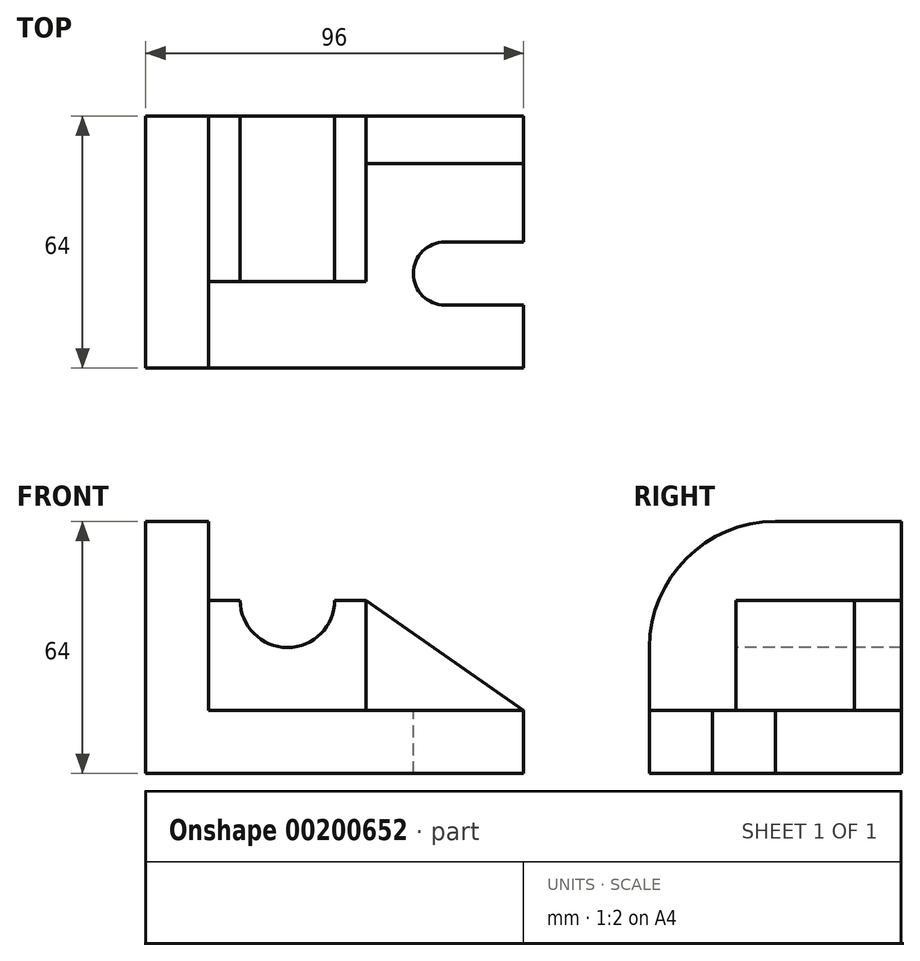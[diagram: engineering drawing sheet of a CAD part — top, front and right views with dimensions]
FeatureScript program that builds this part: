
annotation { "Feature Type Name" : "Feature", "Feature Type Description" : "" }
export const myFeature = defineFeature(function(context is Context, id is Id, definition is map)
    precondition{}
    {
        {
            var Q0;
            Q0=qCreatedBy(makeId("Front.planeOp"),FACE);
            var sketch = newSketch(context, id + "F0", { "sketchPlane" : qUnion([Q0])});
            skLineSegment(sketch, "E0.bottom", {"start": v(-41.26, -23.63) * mm, "end": v(54.74, -23.63) * mm});
            skLineSegment(sketch, "E0.top", {"start": v(-41.26, -39.63) * mm, "end": v(54.74, -39.63) * mm});
            skLineSegment(sketch, "E0.left", {"start": v(-41.26, -23.63) * mm, "end": v(-41.26, -39.63) * mm});
            skLineSegment(sketch, "E0.right", {"start": v(54.74, -23.63) * mm, "end": v(54.74, -39.63) * mm});
            skLineSegment(sketch, "E1.bottom", {"start": v(-41.26, -23.63) * mm, "end": v(-25.26, -23.63) * mm});
            skLineSegment(sketch, "E1.top", {"start": v(-41.26, 24.37) * mm, "end": v(-25.26, 24.37) * mm});
            skLineSegment(sketch, "E1.left", {"start": v(-41.26, -23.63) * mm, "end": v(-41.26, 24.37) * mm});
            skLineSegment(sketch, "E1.right", {"start": v(-25.26, -23.63) * mm, "end": v(-25.26, 24.37) * mm});
            skSolve(sketch);
        }
        {
            var Q0;
            Q0 = qSketchRegion(id + "F0", true);
            extrude(context, id + "F1", {"entities" : qUnion([Q0]), "depth" : 64 * mm});
        }
        {
            var Q0;
            Q0=makeQuery(id+"F1.opExtrude","CAP_EDGE",EDGE,{"disambiguationData":[OSD([sQuery(id+"F0.wireOp",EDGE,"E1.top")])],"isStart":false});
            fillet(context, id + "F2", {"entities" : qUnion([Q0]), "radius" : 32 * mm, "tangentPropagation" : true, "allowEdgeOverflow" : false});
        }
        {
            var Q0;
            Q0=makeQuery(id+"F1.opExtrude","SWEPT_FACE",FACE,{"disambiguationData":[OSD([sQuery(id+"F0.wireOp",EDGE,"E0.bottom")])]});
            var sketch = newSketch(context, id + "F3", { "sketchPlane" : qUnion([Q0])});
            skArc(sketch, "E2", {"start": v(34.74, -32) * mm, "mid": v(26.74, -40) * mm, "end": v(34.74, -48) * mm});
            skLineSegment(sketch, "E3.bottom", {"start": v(54.74, -32) * mm, "end": v(34.74, -32) * mm});
            skLineSegment(sketch, "E3.top", {"start": v(54.74, -48) * mm, "end": v(34.74, -48) * mm});
            skLineSegment(sketch, "E3.left", {"start": v(54.74, -32) * mm, "end": v(54.74, -48) * mm});
            skPoint(sketch, "E3.right.end.orphan", {"position": v(14.74, -48) * mm});
            skPoint(sketch, "E3.right.start.orphan", {"position": v(14.74, -32) * mm});
            skLineSegment(sketch, "E4.bottom", {"start": v(-25.26, 0) * mm, "end": v(14.74, 0) * mm});
            skLineSegment(sketch, "E4.top", {"start": v(-25.26, -42) * mm, "end": v(14.74, -42) * mm});
            skLineSegment(sketch, "E4.left", {"start": v(-25.26, 0) * mm, "end": v(-25.26, -42) * mm});
            skLineSegment(sketch, "E4.right", {"start": v(14.74, 0) * mm, "end": v(14.74, -42) * mm});
            skSolve(sketch);
        }
        {
            var Q0;
            Q0=makeQuery(id+"F3.imprint","IMPRINT",FACE,{"disambiguationData":[TD([[makeQuery(id+"F3.imprint","IMPRINT",EDGE,{"derivedFrom":sQuery(id+"F3.wireOp",EDGE,"E2")}),1.0]])]});
            extrude(context, id + "F4", {"entities" : qUnion([Q0]), "operationType" : NewBodyOperationType.REMOVE, "endBound" : BoundingType.UP_TO_NEXT, "oppositeDirection" : true, "depth" : 25 * mm});
        }
        {
            var Q0;
            Q0=makeQuery(id+"F3.imprint","IMPRINT",FACE,{"disambiguationData":[TD([[makeQuery(id+"F3.imprint","IMPRINT",EDGE,{"derivedFrom":sQuery(id+"F3.wireOp",EDGE,"E4.bottom")}),-1.0]])]});
            extrude(context, id + "F5", {"entities" : qUnion([Q0]), "operationType" : NewBodyOperationType.ADD, "depth" : 28 * mm});
        }
        {
            var Q0;
            Q0=makeQuery(id+"F5.opExtrude","SWEPT_FACE",FACE,{"disambiguationData":[OSD([sQuery(id+"F3.wireOp",EDGE,"E4.top")])]});
            var sketch = newSketch(context, id + "F6", { "sketchPlane" : qUnion([Q0])});
            skCircle(sketch, "E5", {"center": v(-5.26, 4.37) * mm, "radius": 12 * mm});
            skSolve(sketch);
        }
        {
            var Q0;
            {var subQ0=sQuery(id+"F6.wireOp",EDGE,"E5");var subQ1=makeQuery(id+"F5.opExtrude","CAP_EDGE",EDGE,{"disambiguationData":[OSD([sQuery(id+"F3.wireOp",EDGE,"E4.top")])],"isStart":false});var subQ2=makeQuery(id+"F6.imprint","INTERSECT",VERTEX,{"disambiguationData":[OD(0.0)],"derivedFrom":[subQ1,subQ0]});Q0=makeQuery(id+"F6.imprint","IMPRINT",FACE,{"disambiguationData":[TD([[makeQuery(id+"F6.imprint","IMPRINT",EDGE,{"disambiguationData":[TD([[subQ2,1.0]])],"derivedFrom":subQ0}),1.0]])]});}
            extrude(context, id + "F7", {"entities" : qUnion([Q0]), "operationType" : NewBodyOperationType.REMOVE, "oppositeDirection" : true, "depth" : 42 * mm, "hasSecondDirection" : true, "secondDirectionOppositeDirection" : false, "secondDirectionDepth" : 25 * mm});
        }
        {
            var Q0;
            Q0=makeQuery(id+"F5.boolean.opBoolean","MERGE",FACE,{"derivedFrom":[makeQuery(id+"F1.opExtrude","CAP_FACE",FACE,{"disambiguationData":[OSD([sQuery(id+"F0.wireOp",EDGE,"E0.bottom"),sQuery(id+"F0.wireOp",EDGE,"E0.top"),sQuery(id+"F0.wireOp",EDGE,"E0.left"),sQuery(id+"F0.wireOp",EDGE,"E0.right"),sQuery(id+"F0.wireOp",EDGE,"E1.top"),sQuery(id+"F0.wireOp",EDGE,"E1.left"),sQuery(id+"F0.wireOp",EDGE,"E1.right")])],"isStart":true}),makeQuery(id+"F5.opExtrude","SWEPT_FACE",FACE,{"disambiguationData":[OSD([sQuery(id+"F3.wireOp",EDGE,"E4.bottom")])]})]});
            var sketch = newSketch(context, id + "F8", { "sketchPlane" : qUnion([Q0])});
            skLineSegment(sketch, "E6", {"start": v(-14.74, 4.37) * mm, "end": v(-54.74, -23.63) * mm});
            skSolve(sketch);
        }
        {
            var Q0;
            Q0 = qSketchRegion(id + "F8", true);
            var Q1;
            Q1=makeQuery(id+"F8.imprint","IMPRINT",FACE,{"disambiguationData":[TD([[makeQuery(id+"F8.imprint","IMPRINT",EDGE,{"derivedFrom":sQuery(id+"F8.wireOp",EDGE,"E6")}),1.0]])]});
            extrude(context, id + "F9", {"entities" : qUnion([Q0, Q1]), "operationType" : NewBodyOperationType.ADD, "oppositeDirection" : true, "depth" : 12 * mm});
        }
    });
